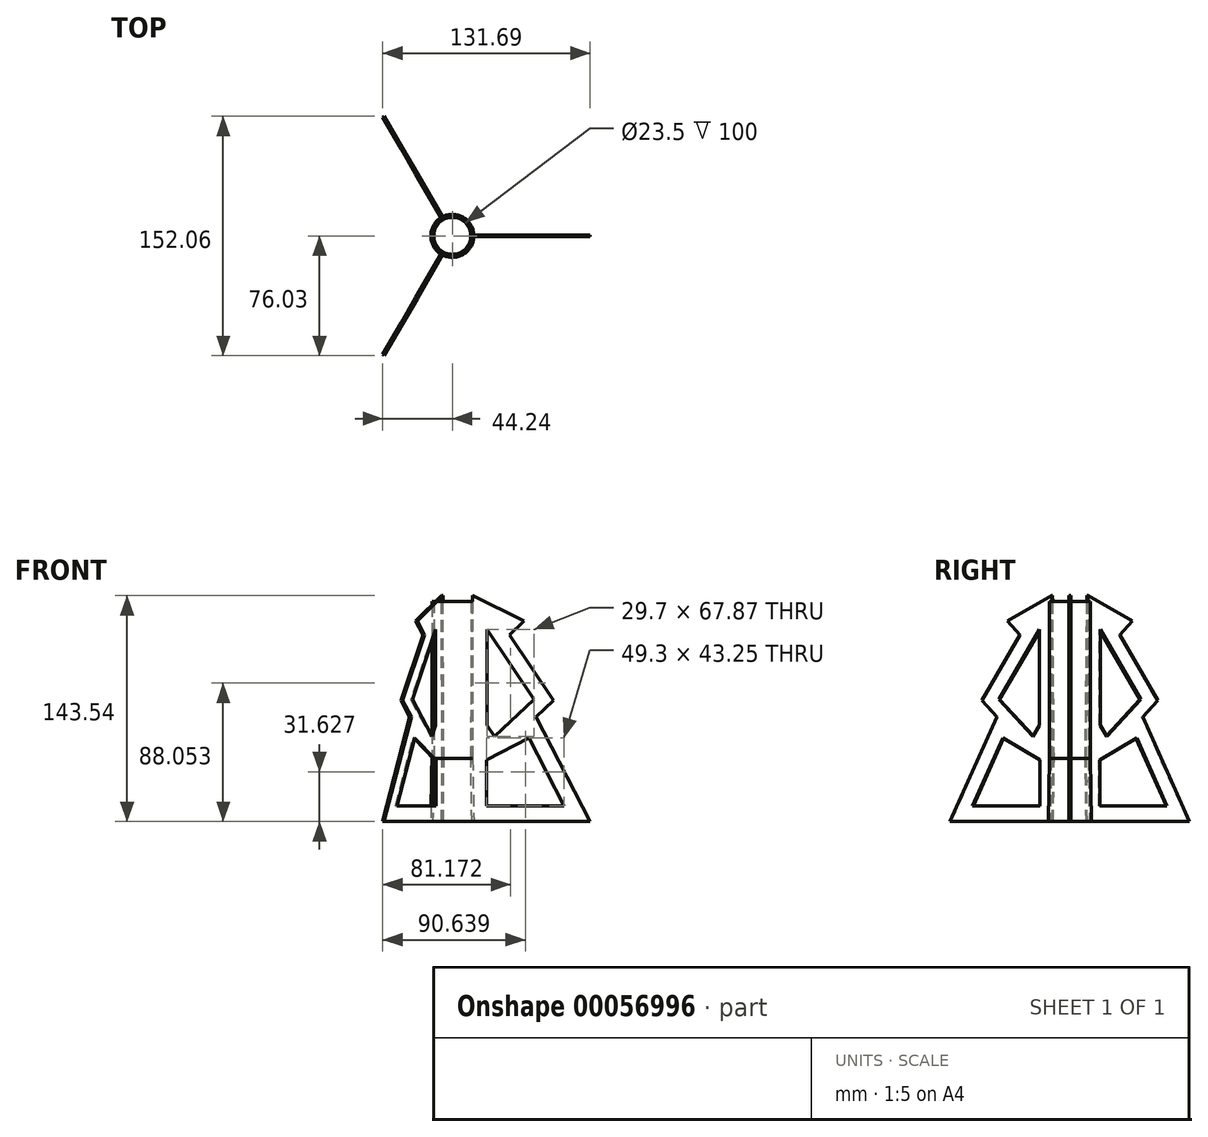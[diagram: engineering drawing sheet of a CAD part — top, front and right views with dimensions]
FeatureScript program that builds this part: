
annotation { "Feature Type Name" : "Feature", "Feature Type Description" : "" }
export const myFeature = defineFeature(function(context is Context, id is Id, definition is map)
    precondition{}
    {
        {
            var Q0;
            Q0=qCreatedBy(makeId("Top.planeOp"),FACE);
            var sketch = newSketch(context, id + "F0", { "sketchPlane" : qUnion([Q0])});
            skCircle(sketch, "E0", {"center": v(0, 0) * mm, "radius": 11.75 * mm});
            skCircle(sketch, "E1", {"center": v(0, 0) * mm, "radius": 12.55 * mm});
            skSolve(sketch);
        }
        {
            var Q0;
            Q0=qCreatedBy(makeId("Front.planeOp"),FACE);
            var sketch = newSketch(context, id + "F1", { "sketchPlane" : qUnion([Q0])});
            skLineSegment(sketch, "E2", {"start": v(0, 0) * mm, "end": v(0, 40) * mm, "construction": true});
            skLineSegment(sketch, "E3.0", {"start": v(-11.75, 0) * mm, "end": v(11.75, 0) * mm, "construction": true});
            skLineSegment(sketch, "E4.0", {"start": v(-12.55, 0) * mm, "end": v(12.55, 0) * mm, "construction": true});
            skLineSegment(sketch, "E5", {"start": v(11.75, 0) * mm, "end": v(11.75, 40) * mm, "construction": true});
            skLineSegment(sketch, "E6", {"start": v(11.75, 40) * mm, "end": v(12.45, 0) * mm});
            skLineSegment(sketch, "E7", {"start": v(12.45, 0) * mm, "end": v(13.65, 0.02) * mm});
            skLineSegment(sketch, "E8", {"start": v(13.65, 0.02) * mm, "end": v(12.95, 40) * mm});
            skLineSegment(sketch, "E9", {"start": v(11.75, 40) * mm, "end": v(12.95, 40) * mm});
            skPoint(sketch, "E10.visualSharp", {"position": v(12.95, 40) * mm});
            skLineSegment(sketch, "E10.filletArc", {"start": v(12.95, 40) * mm, "end": v(12.95, 40) * mm});
            skPoint(sketch, "E11.visualSharp", {"position": v(11.75, 40) * mm});
            skLineSegment(sketch, "E11.filletArc", {"start": v(11.75, 40) * mm, "end": v(11.75, 40) * mm});
            skLineSegment(sketch, "E12", {"start": v(11.75, 40) * mm, "end": v(11.75, 140) * mm});
            skLineSegment(sketch, "E13", {"start": v(11.75, 140) * mm, "end": v(12.95, 140) * mm});
            skLineSegment(sketch, "E14", {"start": v(12.95, 140) * mm, "end": v(12.95, 40) * mm});
            skSolve(sketch);
        }
        {
            var Q0;
            Q0=makeQuery(id+"F1.imprint","IMPRINT",FACE,{"disambiguationData":[TD([[makeQuery(id+"F1.imprint","IMPRINT",EDGE,{"derivedFrom":sQuery(id+"F1.wireOp",EDGE,"E6")}),1.0]])]});
            var Q1;
            Q1=makeQuery(id+"F1.imprint","IMPRINT",FACE,{"disambiguationData":[TD([[makeQuery(id+"F1.imprint","IMPRINT",EDGE,{"derivedFrom":sQuery(id+"F1.wireOp",EDGE,"E9")}),1.0]])]});
            var Q2;
            Q2=sQuery(id+"F1.wireOp",EDGE,"E2");
            revolve(context, id + "F2", {"entities" : qUnion([Q0, Q1]), "axis" : qUnion([Q2]), "revolveType" : RevolveType.FULL});
        }
        {
            var Q0;
            Q0=qCreatedBy(makeId("Front.planeOp"),FACE);
            var sketch = newSketch(context, id + "F3", { "sketchPlane" : qUnion([Q0])});
            skLineSegment(sketch, "E15", {"start": v(-13.65, 0.02) * mm, "end": v(-12.95, 39.82) * mm, "construction": true});
            skLineSegment(sketch, "E16", {"start": v(12.95, 39.82) * mm, "end": v(13.65, 0.02) * mm, "construction": true});
            skLineSegment(sketch, "E17", {"start": v(-12.45, 0) * mm, "end": v(-11.75, 39.8) * mm, "construction": true});
            skLineSegment(sketch, "E18", {"start": v(11.78, 38.01) * mm, "end": v(12.45, 0) * mm, "construction": true});
            skLineSegment(sketch, "E19", {"start": v(11.78, 38.01) * mm, "end": v(11.75, 40) * mm, "construction": true});
            skLineSegment(sketch, "E20", {"start": v(12.45, 0) * mm, "end": v(87.45, 0) * mm});
            skLineSegment(sketch, "E21", {"start": v(87.45, 0) * mm, "end": v(53.15, 66.59) * mm});
            skLineSegment(sketch, "E22", {"start": v(53.15, 66.59) * mm, "end": v(64.2, 76.9) * mm});
            skLineSegment(sketch, "E23", {"start": v(64.2, 76.9) * mm, "end": v(36.28, 118.72) * mm});
            skLineSegment(sketch, "E24", {"start": v(36.28, 118.72) * mm, "end": v(45.5, 127.33) * mm});
            skLineSegment(sketch, "E25", {"start": v(45.5, 127.33) * mm, "end": v(12.95, 143.54) * mm});
            skLineSegment(sketch, "E26.0", {"start": v(12.95, 40) * mm, "end": v(-12.95, 40) * mm, "construction": true});
            skLineSegment(sketch, "E27", {"start": v(12.45, 0) * mm, "end": v(11.75, 40) * mm});
            skLineSegment(sketch, "E28", {"start": v(11.75, 40) * mm, "end": v(12.95, 143.54) * mm});
            skSolve(sketch);
        }
        {
            var Q0;
            Q0=makeQuery(id+"F3.imprint","IMPRINT",FACE,{"disambiguationData":[TD([[makeQuery(id+"F3.imprint","IMPRINT",EDGE,{"derivedFrom":sQuery(id+"F3.wireOp",EDGE,"E20")}),1.0]])]});
            extrude(context, id + "F4", {"entities" : qUnion([Q0]), "endBound" : BoundingType.SYMMETRIC, "depth" : 1.2 * mm});
        }
        {
            var Q0;
            Q0=makeQuery(id+"F4.opExtrude","CAP_FACE",FACE,{"disambiguationData":[OSD([sQuery(id+"F3.wireOp",EDGE,"E20"),sQuery(id+"F3.wireOp",EDGE,"E21"),sQuery(id+"F3.wireOp",EDGE,"E22"),sQuery(id+"F3.wireOp",EDGE,"E23"),sQuery(id+"F3.wireOp",EDGE,"E24"),sQuery(id+"F3.wireOp",EDGE,"E25"),sQuery(id+"F3.wireOp",EDGE,"E27"),sQuery(id+"F3.wireOp",EDGE,"E28")])],"isStart":false});
            var sketch = newSketch(context, id + "F5", { "sketchPlane" : qUnion([Q0])});
            skLineSegment(sketch, "E29", {"start": v(71.05, 10) * mm, "end": v(21.75, 10) * mm});
            skLineSegment(sketch, "E30", {"start": v(22.08, 121.99) * mm, "end": v(51.78, 77.48) * mm});
            skPoint(sketch, "E31.endSnap0", {"position": v(58.67, 71.74) * mm});
            skLineSegment(sketch, "E32", {"start": v(51.78, 77.48) * mm, "end": v(26.72, 54.12) * mm});
            skLineSegment(sketch, "E33", {"start": v(26.72, 54.12) * mm, "end": v(22.08, 61.07) * mm});
            skLineSegment(sketch, "E34", {"start": v(22.08, 61.07) * mm, "end": v(22.08, 121.99) * mm});
            skLineSegment(sketch, "E35", {"start": v(21.75, 10) * mm, "end": v(21.75, 39.34) * mm});
            skLineSegment(sketch, "E36", {"start": v(71.05, 10) * mm, "end": v(48.77, 53.25) * mm});
            skLineSegment(sketch, "E37", {"start": v(48.77, 53.25) * mm, "end": v(21.75, 39.34) * mm});
            skSolve(sketch);
        }
        {
            var Q0;
            Q0=makeQuery(id+"F5.imprint","IMPRINT",FACE,{"disambiguationData":[TD([[makeQuery(id+"F5.imprint","IMPRINT",EDGE,{"derivedFrom":sQuery(id+"F5.wireOp",EDGE,"YT4zo8UA-HXXk-e8u7-XbN5-Sr3b6glm5Ujn")}),1.0]])]});
            var Q1;
            Q1=makeQuery(id+"F5.imprint","IMPRINT",FACE,{"disambiguationData":[TD([[makeQuery(id+"F5.imprint","IMPRINT",EDGE,{"derivedFrom":sQuery(id+"F5.wireOp",EDGE,"E29")}),-1.0]])]});
            var Q2;
            Q2=makeQuery(id+"F5.imprint","IMPRINT",FACE,{"disambiguationData":[TD([[makeQuery(id+"F5.imprint","IMPRINT",EDGE,{"derivedFrom":sQuery(id+"F5.wireOp",EDGE,"E30")}),-1.0]])]});
            extrude(context, id + "F6", {"entities" : qUnion([Q0, Q1, Q2]), "operationType" : NewBodyOperationType.REMOVE, "endBound" : BoundingType.THROUGH_ALL, "oppositeDirection" : true, "depth" : 25 * mm});
        }
        {
            var Q0;
            Q0=makeQuery(id+"F4.opExtrude","SWEPT_BODY",BODY,{"disambiguationData":[OSD([sQuery(id+"F3.wireOp",EDGE,"E20"),sQuery(id+"F3.wireOp",EDGE,"E21"),sQuery(id+"F3.wireOp",EDGE,"E22"),sQuery(id+"F3.wireOp",EDGE,"E23"),sQuery(id+"F3.wireOp",EDGE,"E24"),sQuery(id+"F3.wireOp",EDGE,"E25"),sQuery(id+"F3.wireOp",EDGE,"dSGhwxRR-ejtS-kXEd-Wm1k-lLYw4eHastu8")])]});
            var Q1;
            Q1=sQuery(id+"F1.wireOp",EDGE,"E2");
            circularPattern(context, id + "F7", {"entities" : qUnion([Q0]), "axis" : qUnion([Q1]), "angle" : 360 * degree, "instanceCount" : round(3), "equalSpace" : true});
        }
    });
